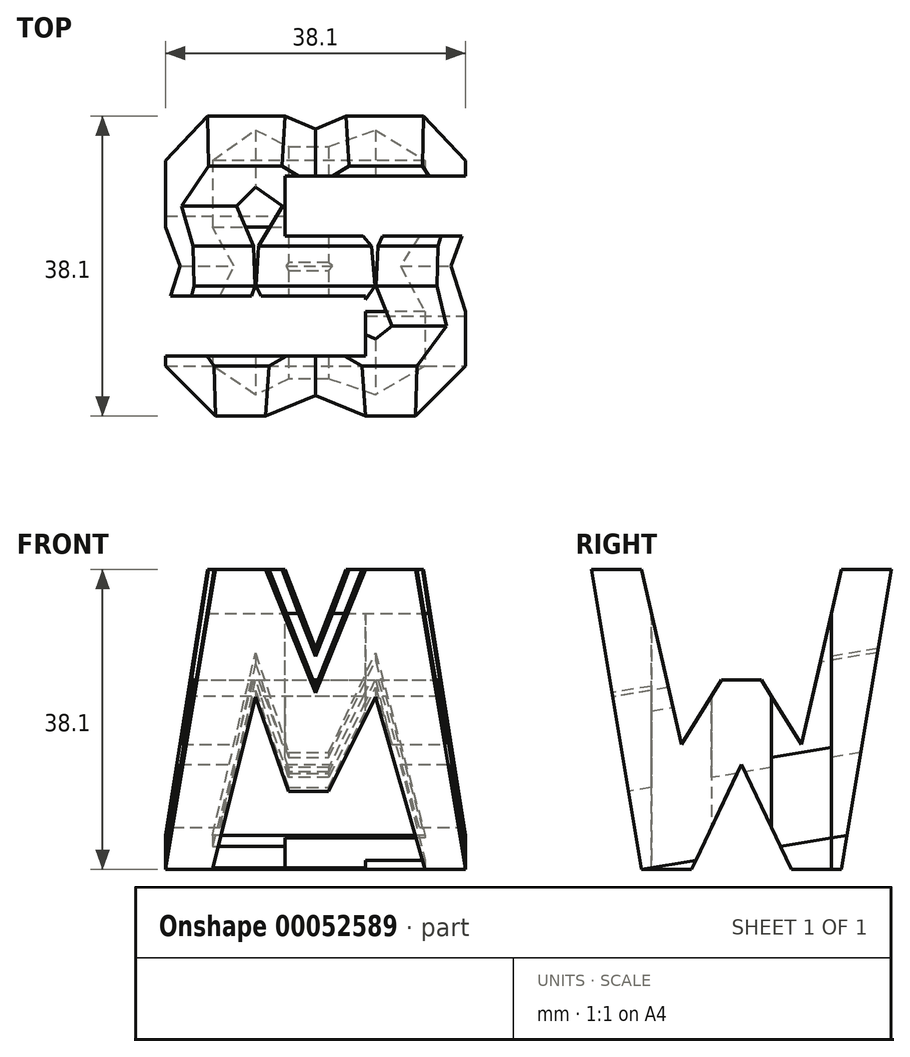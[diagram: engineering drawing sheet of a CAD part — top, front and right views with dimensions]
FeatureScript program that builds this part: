
annotation { "Feature Type Name" : "Feature", "Feature Type Description" : "" }
export const myFeature = defineFeature(function(context is Context, id is Id, definition is map)
    precondition{}
    {
        {
            var Q0;
            Q0=qCreatedBy(makeId("Front.planeOp"),FACE);
            var sketch = newSketch(context, id + "F0", { "sketchPlane" : qUnion([Q0])});
            skLineSegment(sketch, "E0.bottom", {"start": v(0, 0) * mm, "end": v(38.1, 0) * mm});
            skLineSegment(sketch, "E0.top", {"start": v(0, 38.1) * mm, "end": v(38.1, 38.1) * mm});
            skLineSegment(sketch, "E0.left", {"start": v(0, 0) * mm, "end": v(0, 38.1) * mm});
            skLineSegment(sketch, "E0.right", {"start": v(38.1, 0) * mm, "end": v(38.1, 38.1) * mm});
            skSolve(sketch);
        }
        {
            var Q0;
            Q0=makeQuery(id+"F0.imprint","IMPRINT",FACE,{"disambiguationData":[TD([[makeQuery(id+"F0.imprint","IMPRINT",EDGE,{"derivedFrom":sQuery(id+"F0.wireOp",EDGE,"E0.bottom")}),1.0]])]});
            extrude(context, id + "F1", {"entities" : qUnion([Q0]), "depth" : 38.1 * mm});
        }
        {
            var Q0;
            Q0=qCreatedBy(makeId("Right.planeOp"),FACE);
            cPlane(context, id + "F2", {"entities" : qUnion([Q0]), "cplaneType" : CPlaneType.OFFSET, "offset" : 38.1 * mm, "width" : 152.4 * mm, "height" : 152.4 * mm});
        }
        {
            var Q0;
            Q0=qCreatedBy(makeId("Top.planeOp"),FACE);
            cPlane(context, id + "F3", {"entities" : qUnion([Q0]), "cplaneType" : CPlaneType.OFFSET, "offset" : 38.1 * mm, "width" : 152.4 * mm, "height" : 152.4 * mm});
        }
        {
            var Q0;
            Q0=qCreatedBy(id+"F2.planeOp",FACE);
            var sketch = newSketch(context, id + "F4", { "sketchPlane" : qUnion([Q0])});
            skLineSegment(sketch, "E1.bottom", {"start": v(0, 0) * mm, "end": v(-38.1, 0) * mm});
            skLineSegment(sketch, "E1.top", {"start": v(0, 38.1) * mm, "end": v(-38.1, 38.1) * mm});
            skLineSegment(sketch, "E1.left", {"start": v(0, 0) * mm, "end": v(0, 38.1) * mm});
            skLineSegment(sketch, "E1.right", {"start": v(-38.1, 0) * mm, "end": v(-38.1, 38.1) * mm});
            skLineSegment(sketch, "E2", {"start": v(-38.1, 38.1) * mm, "end": v(-31.75, 0) * mm});
            skLineSegment(sketch, "E3", {"start": v(-31.75, 0) * mm, "end": v(-25.4, 0) * mm});
            skLineSegment(sketch, "E4", {"start": v(-25.4, 0) * mm, "end": v(-19.05, 13.36) * mm});
            skLineSegment(sketch, "E5", {"start": v(-19.05, 13.36) * mm, "end": v(-12.7, 0) * mm});
            skLineSegment(sketch, "E6", {"start": v(-12.7, 0) * mm, "end": v(-6.35, 0) * mm});
            skLineSegment(sketch, "E7", {"start": v(-6.35, 0) * mm, "end": v(0, 38.1) * mm});
            skLineSegment(sketch, "E8", {"start": v(-6.35, 38.1) * mm, "end": v(-11.43, 15.87) * mm});
            skLineSegment(sketch, "E9", {"start": v(-11.43, 15.88) * mm, "end": v(-16.5, 24.04) * mm});
            skLineSegment(sketch, "E10", {"start": v(-16.5, 24.04) * mm, "end": v(-21.59, 24.04) * mm});
            skLineSegment(sketch, "E11", {"start": v(-21.59, 24.04) * mm, "end": v(-26.67, 15.88) * mm});
            skLineSegment(sketch, "E12", {"start": v(-26.67, 15.87) * mm, "end": v(-31.75, 38.1) * mm});
            skSolve(sketch);
        }
        {
            var Q0;
            {var subQ0=sQuery(id+"F4.wireOp",EDGE,"E8");Q0=makeQuery(id+"F4.imprint","IMPRINT",FACE,{"disambiguationData":[TD([[makeQuery(id+"F4.imprint","IMPRINT",EDGE,{"derivedFrom":subQ0}),-1.0]])]});}
            var Q1;
            {var subQ0=sQuery(id+"F4.wireOp",EDGE,"E1.left");Q1=makeQuery(id+"F4.imprint","IMPRINT",FACE,{"disambiguationData":[TD([[makeQuery(id+"F4.imprint","IMPRINT",EDGE,{"derivedFrom":subQ0}),1.0]])]});}
            var Q2;
            {var subQ0=sQuery(id+"F4.wireOp",EDGE,"E4");Q2=makeQuery(id+"F4.imprint","IMPRINT",FACE,{"disambiguationData":[TD([[makeQuery(id+"F4.imprint","IMPRINT",EDGE,{"derivedFrom":subQ0}),-1.0]])]});}
            var Q3;
            {var subQ0=sQuery(id+"F4.wireOp",EDGE,"E1.right");Q3=makeQuery(id+"F4.imprint","IMPRINT",FACE,{"disambiguationData":[TD([[makeQuery(id+"F4.imprint","IMPRINT",EDGE,{"derivedFrom":subQ0}),-1.0]])]});}
            extrude(context, id + "F5", {"entities" : qUnion([Q0, Q1, Q2, Q3]), "operationType" : NewBodyOperationType.REMOVE, "oppositeDirection" : true, "depth" : 49.4 * mm});
        }
        {
            var Q0;
            Q0=makeQuery(id+"F5.boolean.opBoolean","COPY",FACE,{"derivedFrom":makeQuery(id+"F5.opExtrude","SWEPT_FACE",FACE,{"disambiguationData":[OSD([sQuery(id+"F4.wireOp",EDGE,"E2")])]})});
            var sketch = newSketch(context, id + "F6", { "sketchPlane" : qUnion([Q0])});
            skLineSegment(sketch, "E13", {"start": v(12.7, 43.85) * mm, "end": v(19.05, 27.97) * mm});
            skLineSegment(sketch, "E14", {"start": v(19.05, 27.97) * mm, "end": v(25.4, 43.85) * mm});
            skLineSegment(sketch, "E15", {"start": v(25.4, 43.85) * mm, "end": v(31.75, 43.85) * mm});
            skLineSegment(sketch, "E16", {"start": v(31.75, 43.85) * mm, "end": v(38.1, 5.22) * mm});
            skLineSegment(sketch, "E17", {"start": v(38.1, 5.22) * mm, "end": v(32.97, 5.22) * mm});
            skLineSegment(sketch, "E18", {"start": v(32.97, 5.22) * mm, "end": v(26.67, 27.44) * mm});
            skLineSegment(sketch, "E19", {"start": v(26.67, 27.44) * mm, "end": v(20.71, 15.27) * mm});
            skLineSegment(sketch, "E20", {"start": v(20.71, 15.27) * mm, "end": v(15.63, 15.27) * mm});
            skLineSegment(sketch, "E21", {"start": v(15.63, 15.27) * mm, "end": v(11.43, 27.44) * mm});
            skLineSegment(sketch, "E22", {"start": v(11.43, 27.44) * mm, "end": v(5.95, 5.22) * mm});
            skLineSegment(sketch, "E23", {"start": v(5.95, 5.22) * mm, "end": v(0, 5.22) * mm});
            skLineSegment(sketch, "E24", {"start": v(0, 5.22) * mm, "end": v(6.35, 43.85) * mm});
            skLineSegment(sketch, "E25", {"start": v(6.35, 43.85) * mm, "end": v(12.7, 43.85) * mm});
            skSolve(sketch);
        }
        {
            var Q0;
            {var subQ0=sQuery(id+"F6.wireOp",EDGE,"E24");Q0=makeQuery(id+"F6.imprint","IMPRINT",FACE,{"disambiguationData":[TD([[makeQuery(id+"F6.imprint","IMPRINT",EDGE,{"derivedFrom":subQ0}),1.0]])]});}
            var Q1;
            {var subQ0=sQuery(id+"F6.wireOp",EDGE,"E13");Q1=makeQuery(id+"F6.imprint","IMPRINT",FACE,{"disambiguationData":[TD([[makeQuery(id+"F6.imprint","IMPRINT",EDGE,{"derivedFrom":subQ0}),1.0]])]});}
            var Q2;
            {var subQ0=sQuery(id+"F6.wireOp",EDGE,"E16");Q2=makeQuery(id+"F6.imprint","IMPRINT",FACE,{"disambiguationData":[TD([[makeQuery(id+"F6.imprint","IMPRINT",EDGE,{"derivedFrom":subQ0}),1.0]])]});}
            var Q3;
            {var subQ0=sQuery(id+"F6.wireOp",EDGE,"E18");Q3=makeQuery(id+"F6.imprint","IMPRINT",FACE,{"disambiguationData":[TD([[makeQuery(id+"F6.imprint","IMPRINT",EDGE,{"derivedFrom":subQ0}),1.0]])]});}
            extrude(context, id + "F7", {"entities" : qUnion([Q0, Q1, Q2, Q3]), "operationType" : NewBodyOperationType.REMOVE, "oppositeDirection" : true, "depth" : 61.12 * mm});
        }
        {
            var Q0;
            Q0=qCreatedBy(id+"F3.planeOp",FACE);
            var sketch = newSketch(context, id + "F8", { "sketchPlane" : qUnion([Q0])});
            skLineSegment(sketch, "E26", {"start": v(15.19, -7.62) * mm, "end": v(38.76, -7.62) * mm});
            skLineSegment(sketch, "E27", {"start": v(38.76, -7.62) * mm, "end": v(38.76, -15.24) * mm});
            skLineSegment(sketch, "E28", {"start": v(38.76, -15.24) * mm, "end": v(15.19, -15.24) * mm});
            skLineSegment(sketch, "E29", {"start": v(15.19, -15.24) * mm, "end": v(15.19, -7.62) * mm});
            skLineSegment(sketch, "E30", {"start": v(0, -30.48) * mm, "end": v(25.4, -30.48) * mm});
            skLineSegment(sketch, "E31", {"start": v(25.4, -30.48) * mm, "end": v(25.4, -22.86) * mm});
            skLineSegment(sketch, "E32", {"start": v(25.4, -22.86) * mm, "end": v(0, -22.86) * mm});
            skLineSegment(sketch, "E33", {"start": v(0, -22.86) * mm, "end": v(0, -30.48) * mm});
            skSolve(sketch);
        }
        {
            var Q0;
            Q0=makeQuery(id+"F8.imprint","IMPRINT",FACE,{"disambiguationData":[TD([[makeQuery(id+"F8.imprint","IMPRINT",EDGE,{"derivedFrom":sQuery(id+"F8.wireOp",EDGE,"E26")}),-1.0]])]});
            var Q1;
            Q1=makeQuery(id+"F8.imprint","IMPRINT",FACE,{"disambiguationData":[TD([[makeQuery(id+"F8.imprint","IMPRINT",EDGE,{"derivedFrom":sQuery(id+"F8.wireOp",EDGE,"E30")}),1.0]])]});
            extrude(context, id + "F9", {"entities" : qUnion([Q0, Q1]), "operationType" : NewBodyOperationType.REMOVE, "oppositeDirection" : true, "depth" : 45.9 * mm});
        }
    });
